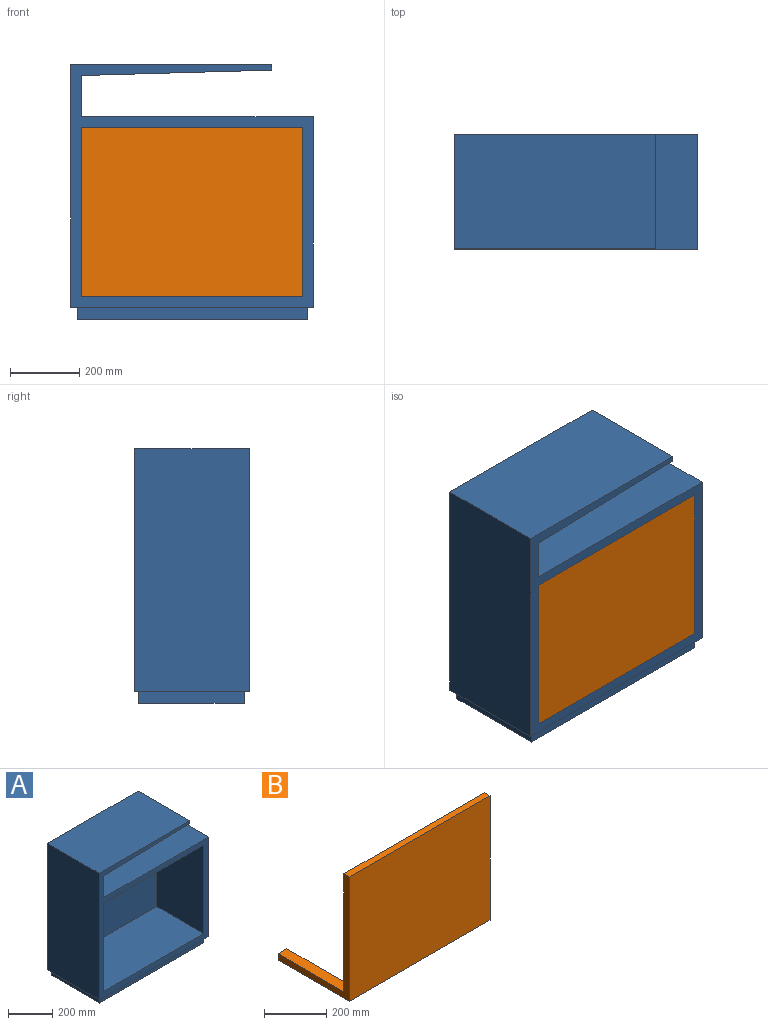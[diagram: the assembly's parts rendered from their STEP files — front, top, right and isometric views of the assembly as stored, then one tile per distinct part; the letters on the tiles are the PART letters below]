
ASSEMBLY  parts=2 mates=1
PART A: 20 faces, bbox 700x330x735 mm
  f0: plane 700x700mm, normal (0,-1,0), area 88851.8mm2, adj f1,f3,f4,f5,f6,f7,f8,f9
  f1: plane 669.58x330mm, normal (0,0,1), area 220961.7mm2, adj f0,f2,f4,f6
  f2: plane 700x700mm, normal (0,1,0), area 402451.8mm2, adj f1,f3,f4,f5,f6,f7,f8,f9
  f3: plane 700x330mm, normal (-1,0,0), area 231000mm2, adj f0,f2,f5,f7
  f4: plane 550x330mm, normal (1,0,0), area 181500mm2, adj f0,f1,f2,f5
  f5: plane 700x330mm, normal (0,0,-1), area 27831.5mm2, adj f0,f2,f3,f4,f15,f16,f17,f18
  f6: plane 330x118.75mm, normal (1,0,0), area 39188.9mm2, adj f0,f1,f2,f9
  f7: plane 580.42x330mm, normal (0,0,1), area 191538.3mm2, adj f0,f2,f3,f8
  f8: plane 330x15.62mm, normal (1,0,0), area 5155.6mm2, adj f0,f2,f7,f9
  f9: plane 550x330mm, normal (0.03,0,-1), area 181573.2mm2, adj f0,f2,f6,f8
  f10: plane 640x300mm, normal (0,0,-1), area 192000mm2, adj f0,f11,f13,f14
  f11: plane 490x300mm, normal (1,0,0), area 147000mm2, adj f0,f10,f12,f14
  f12: plane 640x300mm, normal (0,0,1), area 192000mm2, adj f0,f11,f13,f14
  f13: plane 490x300mm, normal (-1,0,0), area 147000mm2, adj f0,f10,f12,f14
  f14: plane 640x490mm, normal (0,-1,0), area 313600mm2, adj f10,f11,f12,f13
  f15: plane 666.54x35mm, normal (0,-1,0), area 23329mm2, adj f5,f16,f18,f19
  f16: plane 304.81x35mm, normal (-1,0,0), area 10668.3mm2, adj f5,f15,f17,f19
  f17: plane 666.54x35mm, normal (0,1,0), area 23329mm2, adj f5,f16,f18,f19
  f18: plane 304.81x35mm, normal (1,0,0), area 10668.3mm2, adj f5,f15,f17,f19
  f19: plane 666.54x304.81mm, normal (0,0,-1), area 203168.5mm2, adj f15,f16,f17,f18
PART B: 12 faces, bbox 640x325x490 mm
  f0: plane 490x325mm, normal (1,0,0), area 19750mm2, adj f1,f3,f4,f5,f6,f8
  f1: plane 640x25mm, normal (0,0,1), area 16000mm2, adj f0,f2,f4,f5
  f2: plane 490x325mm, normal (-1,0,0), area 19750mm2, adj f1,f3,f4,f5,f9,f11
  f3: plane 640x325mm, normal (0,0,-1), area 40000mm2, adj f0,f2,f4,f5,f7,f8,f10,f11
  f4: plane 640x490mm, normal (0,-1,0), area 313600mm2, adj f0,f1,f2,f3
  f5: plane 640x490mm, normal (0,1,0), area 311600mm2, adj f0,f1,f2,f3,f6,f7,f9,f10
  f6: plane 300x40mm, normal (0,0,1), area 12000mm2, adj f0,f5,f7,f8
  f7: plane 300x25mm, normal (-1,0,0), area 7500mm2, adj f3,f5,f6,f8
  f8: plane 40x25mm, normal (0,1,0), area 1000mm2, adj f0,f3,f6,f7
  f9: plane 300x40mm, normal (0,0,1), area 12000mm2, adj f2,f5,f10,f11
  f10: plane 300x25mm, normal (1,0,0), area 7500mm2, adj f3,f5,f9,f11
  f11: plane 40x25mm, normal (0,1,0), area 1000mm2, adj f2,f3,f9,f10
PLACE A t=(-322.18,73.97,12.47)mm fixed
PLACE B t=(-324.79,-66.03,287.47)mm
MATE slider A.f0 <-> B.f11  axis (0,-1,0) through (-642.18,-91.03,42.47)mm
